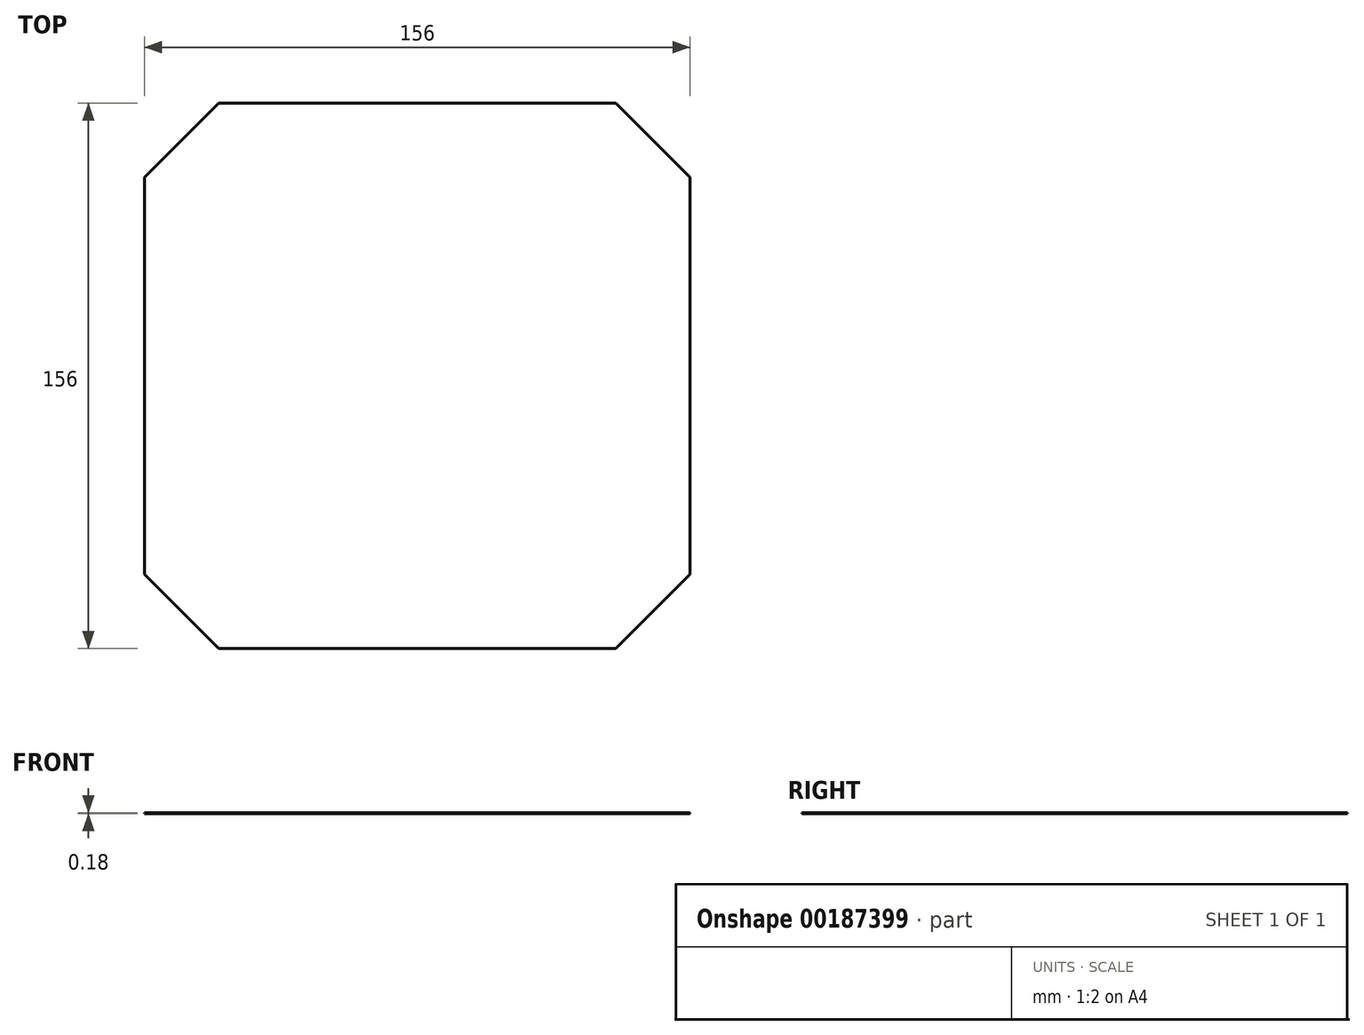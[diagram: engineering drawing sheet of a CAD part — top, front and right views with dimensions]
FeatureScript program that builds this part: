
annotation { "Feature Type Name" : "Feature", "Feature Type Description" : "" }
export const myFeature = defineFeature(function(context is Context, id is Id, definition is map)
    precondition{}
    {
        {
            var Q0;
            Q0=qCreatedBy(makeId("Top.planeOp"),FACE);
            var sketch = newSketch(context, id + "F0", { "sketchPlane" : qUnion([Q0])});
            skLineSegment(sketch, "E0.bottom", {"start": v(78, -78) * mm, "end": v(-78, -78) * mm});
            skLineSegment(sketch, "E0.top", {"start": v(78, 78) * mm, "end": v(-78, 78) * mm});
            skLineSegment(sketch, "E0.left", {"start": v(78, -78) * mm, "end": v(78, 78) * mm});
            skLineSegment(sketch, "E0.right", {"start": v(-78, -78) * mm, "end": v(-78, 78) * mm});
            skPoint(sketch, "E0.middle", {"position": v(0, 0) * mm});
            skLineSegment(sketch, "E1", {"start": v(-78, -56.79) * mm, "end": v(-56.79, -78) * mm});
            skLineSegment(sketch, "E2", {"start": v(78, -56.79) * mm, "end": v(56.79, -78) * mm});
            skLineSegment(sketch, "E3", {"start": v(-78, 56.79) * mm, "end": v(-56.79, 78) * mm});
            skLineSegment(sketch, "E4", {"start": v(56.79, 78) * mm, "end": v(78, 56.79) * mm});
            skSolve(sketch);
        }
        {
            var Q0;
            {var subQ0=sQuery(id+"F0.wireOp",EDGE,"E1");Q0=makeQuery(id+"F0.imprint","IMPRINT",FACE,{"disambiguationData":[TD([[makeQuery(id+"F0.imprint","IMPRINT",EDGE,{"derivedFrom":subQ0}),1.0]])]});}
            extrude(context, id + "F1", {"entities" : qUnion([Q0]), "depth" : .180 * mm});
        }
    });
